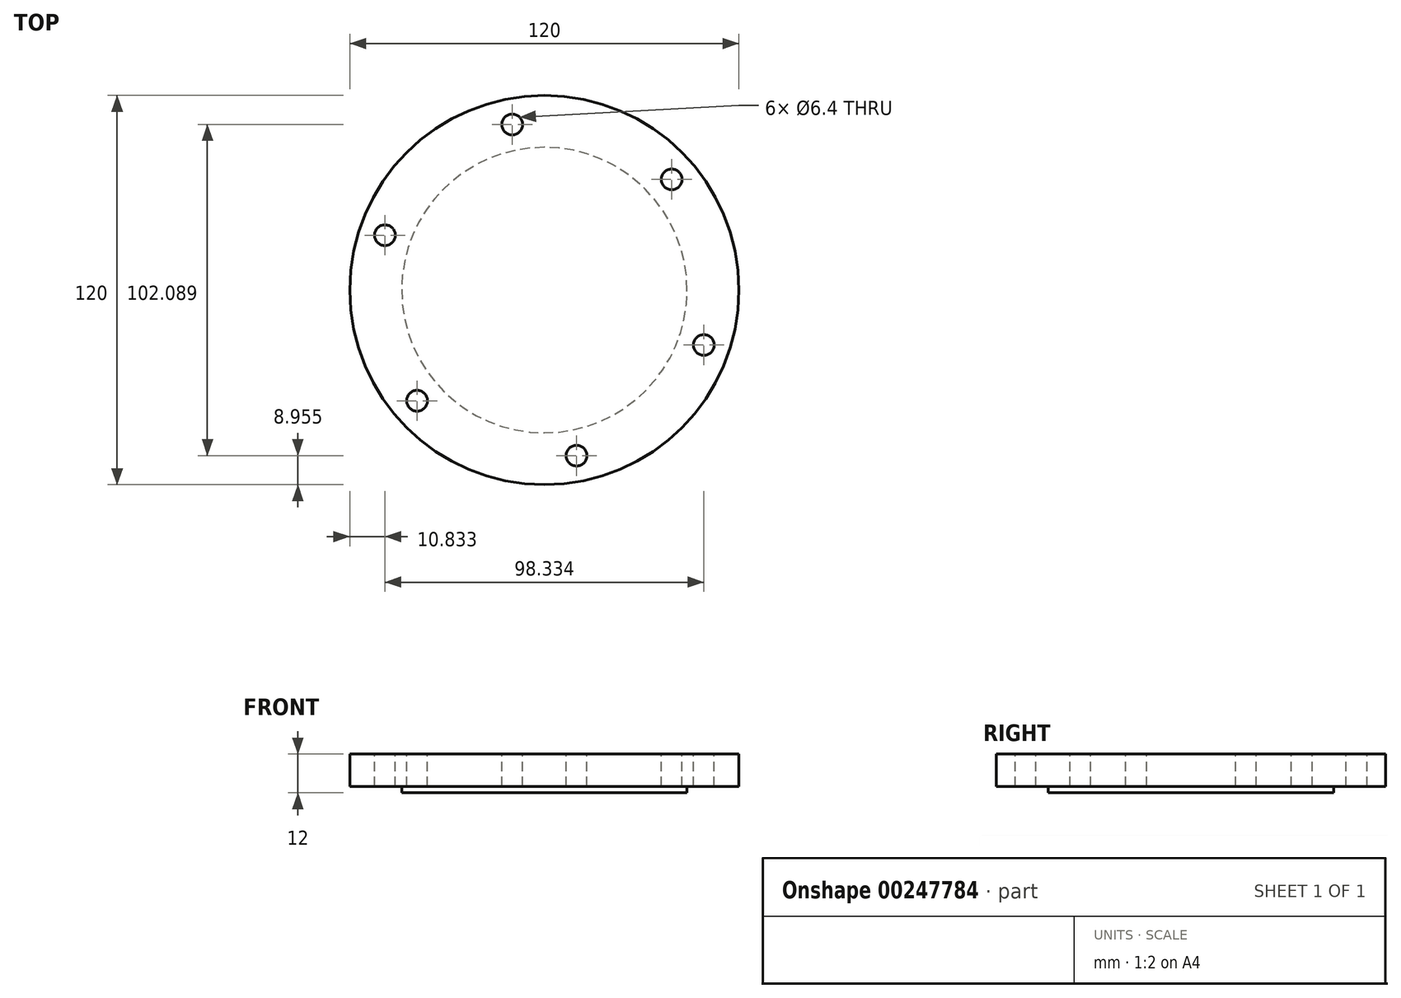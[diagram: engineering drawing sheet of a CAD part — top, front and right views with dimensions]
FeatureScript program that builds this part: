
annotation { "Feature Type Name" : "Feature", "Feature Type Description" : "" }
export const myFeature = defineFeature(function(context is Context, id is Id, definition is map)
    precondition{}
    {
        {
            var Q0;
            Q0=qCreatedBy(makeId("Front.planeOp"),FACE);
            var sketch = newSketch(context, id + "F0", { "sketchPlane" : qUnion([Q0])});
            skLineSegment(sketch, "E0", {"start": v(0, 10) * mm, "end": v(0, -2) * mm});
            skPoint(sketch, "E1", {"position": v(-49.47, 3.56) * mm});
            skLineSegment(sketch, "E2.trimOffspring", {"start": v(-44, -2) * mm, "end": v(-44, 0) * mm});
            skLineSegment(sketch, "E3", {"start": v(-60, 10) * mm, "end": v(-60, 0) * mm});
            skLineSegment(sketch, "E4", {"start": v(-60, 10) * mm, "end": v(0, 10) * mm});
            skLineSegment(sketch, "E5", {"start": v(-44, -2) * mm, "end": v(0, -2) * mm});
            skLineSegment(sketch, "E6", {"start": v(-60, 0) * mm, "end": v(-44, 0) * mm});
            skSolve(sketch);
        }
        {
            var Q0;
            Q0=makeQuery(id+"F0.imprint","IMPRINT",FACE,{"disambiguationData":[TD([[makeQuery(id+"F0.imprint","IMPRINT",EDGE,{"derivedFrom":sQuery(id+"F0.wireOp",EDGE,"E0")}),-1.0]])]});
            var Q1;
            Q1=sQuery(id+"F0.wireOp",EDGE,"E0");
            revolve(context, id + "F1", {"entities" : qUnion([Q0]), "axis" : qUnion([Q1]), "revolveType" : RevolveType.FULL});
        }
        {
            var Q0;
            Q0=makeQuery(id+"F1.opRevolve","SWEPT_FACE",FACE,{"disambiguationData":[OSD([sQuery(id+"F0.wireOp",EDGE,"E4")])]});
            cPlane(context, id + "F2", {"entities" : qUnion([Q0]), "cplaneType" : CPlaneType.OFFSET, "offset" : 0 * mm, "width" : 150 * mm, "height" : 150 * mm});
        }
        {
            var Q0;
            Q0=qCreatedBy(id+"F2.planeOp",FACE);
            var sketch = newSketch(context, id + "F3", { "sketchPlane" : qUnion([Q0])});
            skCircle(sketch, "E7", {"center": v(0, 0) * mm, "radius": 52 * mm, "construction": true});
            skLineSegment(sketch, "E8", {"start": v(0, 0) * mm, "end": v(-18.29, 94.1) * mm, "construction": true});
            skPoint(sketch, "E9", {"position": v(-9.92, 51.04) * mm});
            skPoint(sketch, "E10.1.0", {"position": v(-49.17, 16.93) * mm});
            skPoint(sketch, "E10.2.0", {"position": v(-39.24, -34.12) * mm});
            skPoint(sketch, "E10.3.0", {"position": v(9.92, -51.04) * mm});
            skPoint(sketch, "E10.4.0", {"position": v(49.17, -16.93) * mm});
            skPoint(sketch, "E10.5.0", {"position": v(39.24, 34.12) * mm});
            skSolve(sketch);
        }
        {
            var Q0;
            Q0=sQuery(id+"F3.wireOp",VERTEX,"E9");
            var Q1;
            Q1=sQuery(id+"F3.wireOp",VERTEX,"E10.1.0");
            var Q2;
            Q2=sQuery(id+"F3.wireOp",VERTEX,"E10.2.0");
            var Q3;
            Q3=sQuery(id+"F3.wireOp",VERTEX,"E10.3.0");
            var Q4;
            Q4=sQuery(id+"F3.wireOp",VERTEX,"E10.4.0");
            var Q5;
            Q5=sQuery(id+"F3.wireOp",VERTEX,"E10.5.0");
            var Q6;
            Q6=makeQuery(id+"F1.opRevolve","SWEPT_BODY",BODY,{"disambiguationData":[OSD([sQuery(id+"F0.wireOp",EDGE,"E0"),sQuery(id+"F0.wireOp",EDGE,"E2.trimOffspring"),sQuery(id+"F0.wireOp",EDGE,"E3"),sQuery(id+"F0.wireOp",EDGE,"E4"),sQuery(id+"F0.wireOp",EDGE,"E5"),sQuery(id+"F0.wireOp",EDGE,"E6")])]});
            hole(context, id + "F4", {"style" : HoleStyle.SIMPLE, "endStyle" : HoleEndStyle.THROUGH, "holeDiameter" : 6.4 * mm, "locations" : qUnion([Q0, Q1, Q2, Q3, Q4, Q5]), "scope" : qUnion([Q6]), "isTappedThrough" : true});
        }
    });
